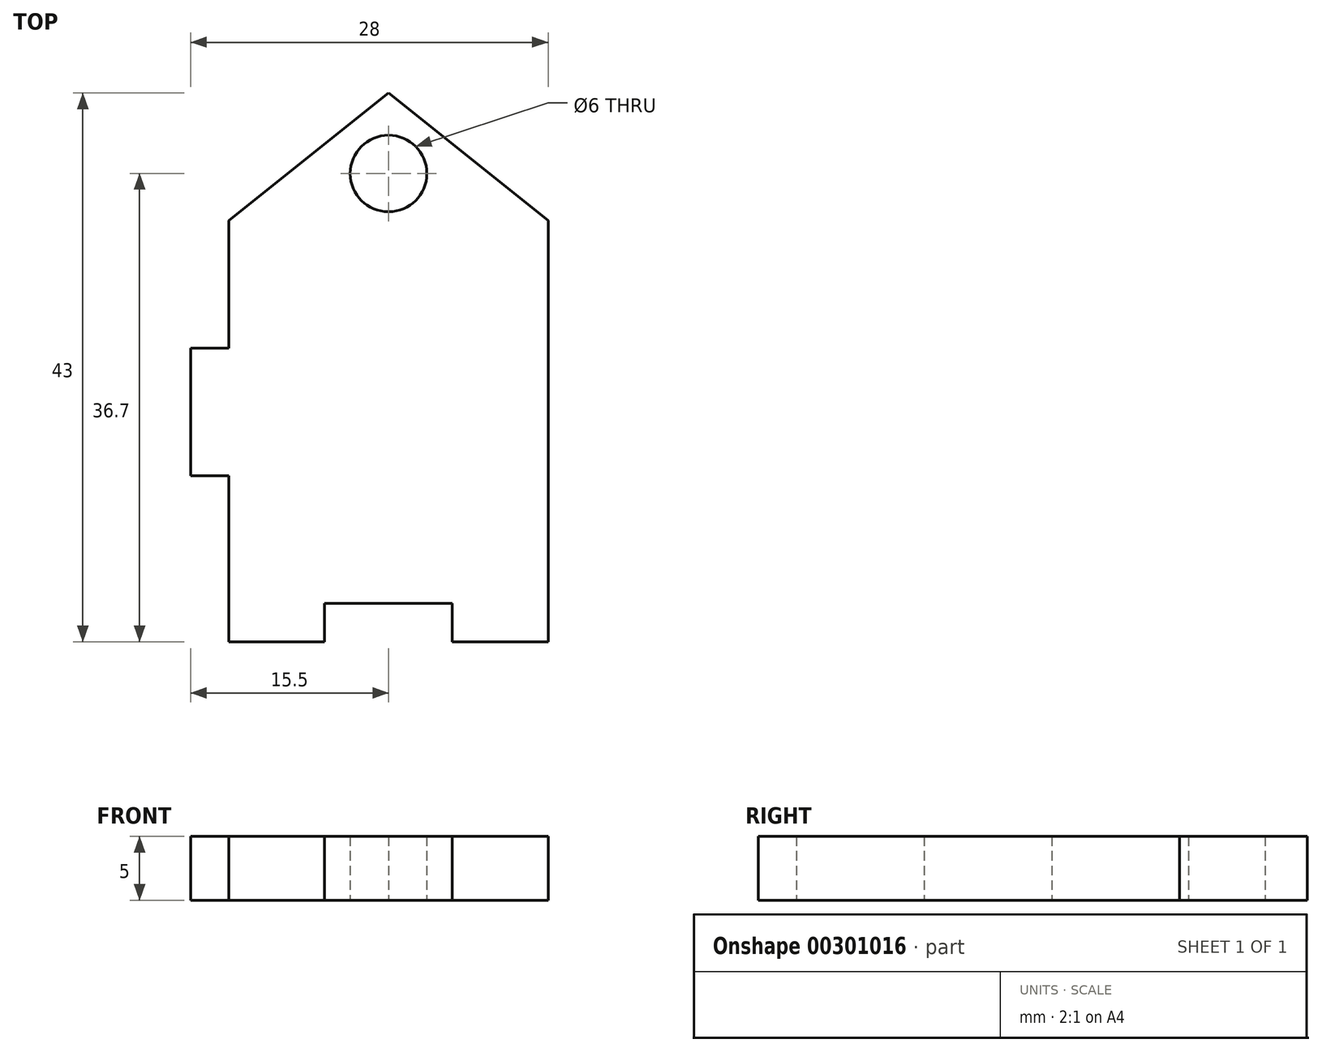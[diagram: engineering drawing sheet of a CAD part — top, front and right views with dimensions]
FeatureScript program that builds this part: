
annotation { "Feature Type Name" : "Feature", "Feature Type Description" : "" }
export const myFeature = defineFeature(function(context is Context, id is Id, definition is map)
    precondition{}
    {
        {
            var Q0;
            Q0=qCreatedBy(makeId("Top.planeOp"),FACE);
            var sketch = newSketch(context, id + "F0", { "sketchPlane" : qUnion([Q0])});
            skCircle(sketch, "E0", {"center": v(0, 0) * mm, "radius": 3 * mm});
            skLineSegment(sketch, "E1", {"start": v(12.5, -36.7) * mm, "end": v(12.5, -3.7) * mm});
            skLineSegment(sketch, "E2", {"start": v(12.5, -3.7) * mm, "end": v(-12.5, -3.7) * mm});
            skLineSegment(sketch, "E3", {"start": v(0, 6.3) * mm, "end": v(-12.5, -3.7) * mm});
            skLineSegment(sketch, "E4", {"start": v(0, 6.3) * mm, "end": v(12.5, -3.7) * mm});
            skLineSegment(sketch, "E5", {"start": v(-12.5, -36.7) * mm, "end": v(-5, -36.7) * mm});
            skLineSegment(sketch, "E6", {"start": v(12.5, -36.7) * mm, "end": v(5, -36.7) * mm});
            skLineSegment(sketch, "E7", {"start": v(-5, -36.7) * mm, "end": v(-5, -33.7) * mm});
            skLineSegment(sketch, "E8", {"start": v(5, -36.7) * mm, "end": v(5, -33.7) * mm});
            skLineSegment(sketch, "E9", {"start": v(-5, -33.7) * mm, "end": v(5, -33.7) * mm});
            skLineSegment(sketch, "E10", {"start": v(-12.5, -3.7) * mm, "end": v(-12.5, -13.7) * mm});
            skLineSegment(sketch, "E11", {"start": v(-12.5, -13.7) * mm, "end": v(-15.5, -13.7) * mm});
            skLineSegment(sketch, "E12", {"start": v(-15.5, -13.7) * mm, "end": v(-15.5, -23.7) * mm});
            skLineSegment(sketch, "E13", {"start": v(-15.5, -23.7) * mm, "end": v(-12.5, -23.7) * mm});
            skLineSegment(sketch, "E14", {"start": v(-12.5, -23.7) * mm, "end": v(-12.5, -36.7) * mm});
            skSolve(sketch);
        }
        {
            var Q0;
            Q0=makeQuery(id+"F0.imprint","IMPRINT",FACE,{"disambiguationData":[TD([[makeQuery(id+"F0.imprint","IMPRINT",EDGE,{"derivedFrom":sQuery(id+"F0.wireOp",EDGE,"E1")}),1.0]])]});
            var Q1;
            Q1=makeQuery(id+"F0.imprint","IMPRINT",FACE,{"disambiguationData":[TD([[makeQuery(id+"F0.imprint","IMPRINT",EDGE,{"derivedFrom":sQuery(id+"F0.wireOp",EDGE,"E0")}),-1.0]])]});
            extrude(context, id + "F1", {"entities" : qUnion([Q0, Q1]), "depth" : 5 * mm, "offsetDistance" : 25 * mm});
        }
    });
